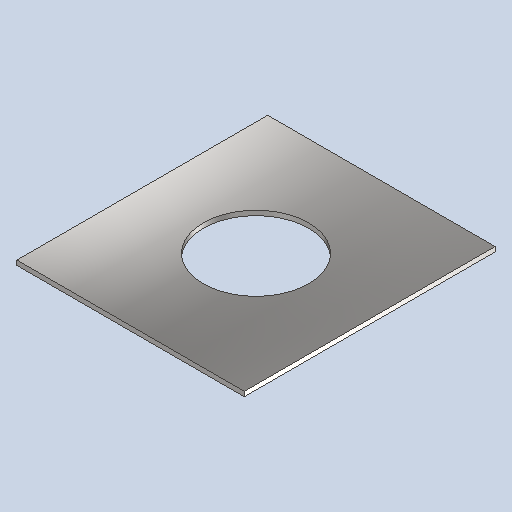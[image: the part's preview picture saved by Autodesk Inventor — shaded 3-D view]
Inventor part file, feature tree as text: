
AUTODESK INVENTOR PART (.ipt)
format: ipt  version: 2025 (Build 290162010, 162A)  size: 140,800 bytes
history: native  units: mm
features: sketch x2, other x2, sheet_metal_op x1, extrude x1
ambient origin geometry x8: Origin, YZ Plane, XZ Plane, XY Plane, X Axis, Y Axis, Z Axis, Center Point
bodies: Solid1 (feature_tree)
feature tree (6):
  sheet_metal_op  "Face1"
  extrude  "Extrusion1"  Depth=214.0mm
  sketch  "Sketch1"  dims[d0=194.0mm d1=214.0mm]
  other  "Plate1"
  sketch  "Sketch2"  dims[d2=4.0mm d3=90.0mm d4=10.0mm d5=0.0mm]
  other  "Definition1"
